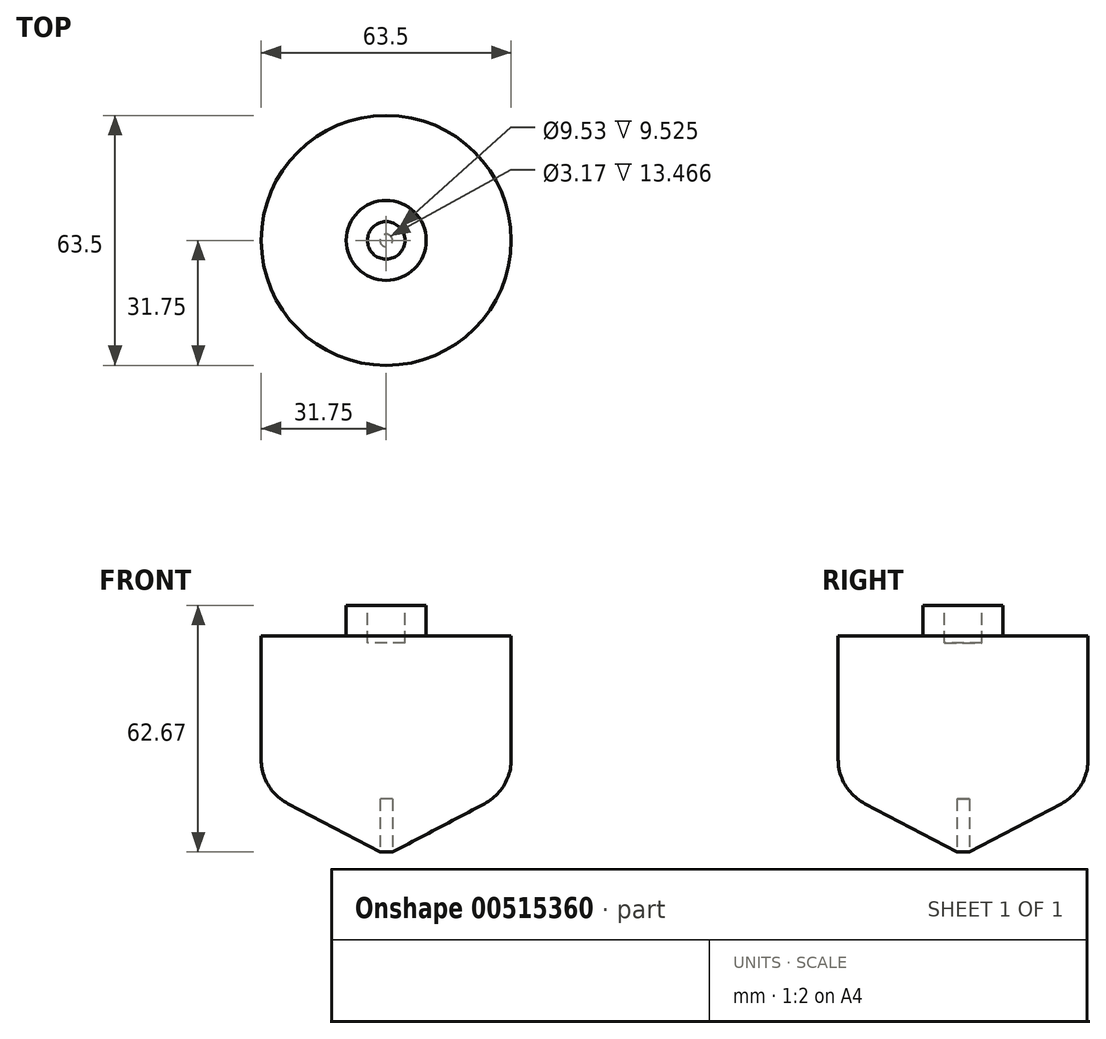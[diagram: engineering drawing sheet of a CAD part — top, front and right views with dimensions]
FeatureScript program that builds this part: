
annotation { "Feature Type Name" : "Feature", "Feature Type Description" : "" }
export const myFeature = defineFeature(function(context is Context, id is Id, definition is map)
    precondition{}
    {
        {
            var Q0;
            Q0=qCreatedBy(makeId("Front.planeOp"),FACE);
            var sketch = newSketch(context, id + "F0", { "sketchPlane" : qUnion([Q0])});
            skLineSegment(sketch, "E0", {"start": v(10.16, 63.5) * mm, "end": v(0, 63.5) * mm});
            skLineSegment(sketch, "E1", {"start": v(0, 63.5) * mm, "end": v(0, 0) * mm});
            skLineSegment(sketch, "E2", {"start": v(31.75, 28.87) * mm, "end": v(31.75, 46.2) * mm});
            skLineSegment(sketch, "E3", {"start": v(0, 0) * mm, "end": v(31.75, 16.69) * mm});
            skLineSegment(sketch, "E4", {"start": v(31.75, 46.2) * mm, "end": v(31.75, 28.87) * mm});
            skLineSegment(sketch, "E5", {"start": v(31.75, 46.2) * mm, "end": v(31.75, 55.76) * mm});
            skLineSegment(sketch, "E6", {"start": v(31.75, 55.76) * mm, "end": v(10.16, 55.76) * mm});
            skLineSegment(sketch, "E7", {"start": v(10.16, 55.76) * mm, "end": v(10.16, 63.5) * mm});
            skLineSegment(sketch, "E8", {"start": v(31.75, 28.87) * mm, "end": v(31.75, 16.69) * mm});
            skSolve(sketch);
        }
        {
            var Q0;
            Q0=qSketchRegion(id+"F0",true);
            var Q1;
            Q1=sQuery(id+"F0.wireOp",EDGE,"E1");
            revolve(context, id + "F1", {"entities" : qUnion([Q0]), "axis" : qUnion([Q1]), "revolveType" : RevolveType.FULL});
        }
        {
            var Q0;
            Q0=makeQuery(id+"F1.opRevolve","SWEPT_FACE",FACE,{"disambiguationData":[OSD([sQuery(id+"F0.wireOp",EDGE,"E0")])]});
            var sketch = newSketch(context, id + "F2", { "sketchPlane" : qUnion([Q0])});
            skCircle(sketch, "E9", {"center": v(0, 0) * mm, "radius": 4.76 * mm});
            skCircle(sketch, "E10", {"center": v(0, -63.96) * mm, "radius": 1.59 * mm});
            skSolve(sketch);
        }
        {
            var Q0;
            Q0=makeQuery(id+"F2.imprint","IMPRINT",FACE,{"disambiguationData":[TD([[makeQuery(id+"F2.imprint","IMPRINT",EDGE,{"derivedFrom":sQuery(id+"F2.wireOp",EDGE,"E9")}),1.0]])]});
            extrude(context, id + "F3", {"entities" : qUnion([Q0]), "operationType" : NewBodyOperationType.REMOVE, "oppositeDirection" : true, "depth" : 9.52 * mm});
        }
        {
            var Q0;
            Q0=qCreatedBy(makeId("Top.planeOp"),FACE);
            var sketch = newSketch(context, id + "F4", { "sketchPlane" : qUnion([Q0])});
            skCircle(sketch, "E11", {"center": v(0, 0) * mm, "radius": 1.59 * mm});
            skSolve(sketch);
        }
        {
            var Q0;
            Q0=makeQuery(id+"F1.opRevolve","SWEPT_EDGE",EDGE,{"disambiguationData":[OSD([sQuery(id+"F0.wireOp",EDGE,"E3"),sQuery(id+"F0.wireOp",EDGE,"E8")])]});
            fillet(context, id + "F5", {"entities" : qUnion([Q0]), "radius" : 12.7 * mm, "tangentPropagation" : true, "allowEdgeOverflow" : false});
        }
        {
            var Q0;
            Q0 = qSketchRegion(id + "F4", true);
            var Q1;
            Q1=sQuery(id+"F4.wireOp",EDGE,"E11");
            extrude(context, id + "F6", {"entities" : qUnion([Q0]), "operationType" : NewBodyOperationType.REMOVE, "surfaceEntities" : qUnion([Q1]), "depth" : 14.3 * mm});
        }
    });
